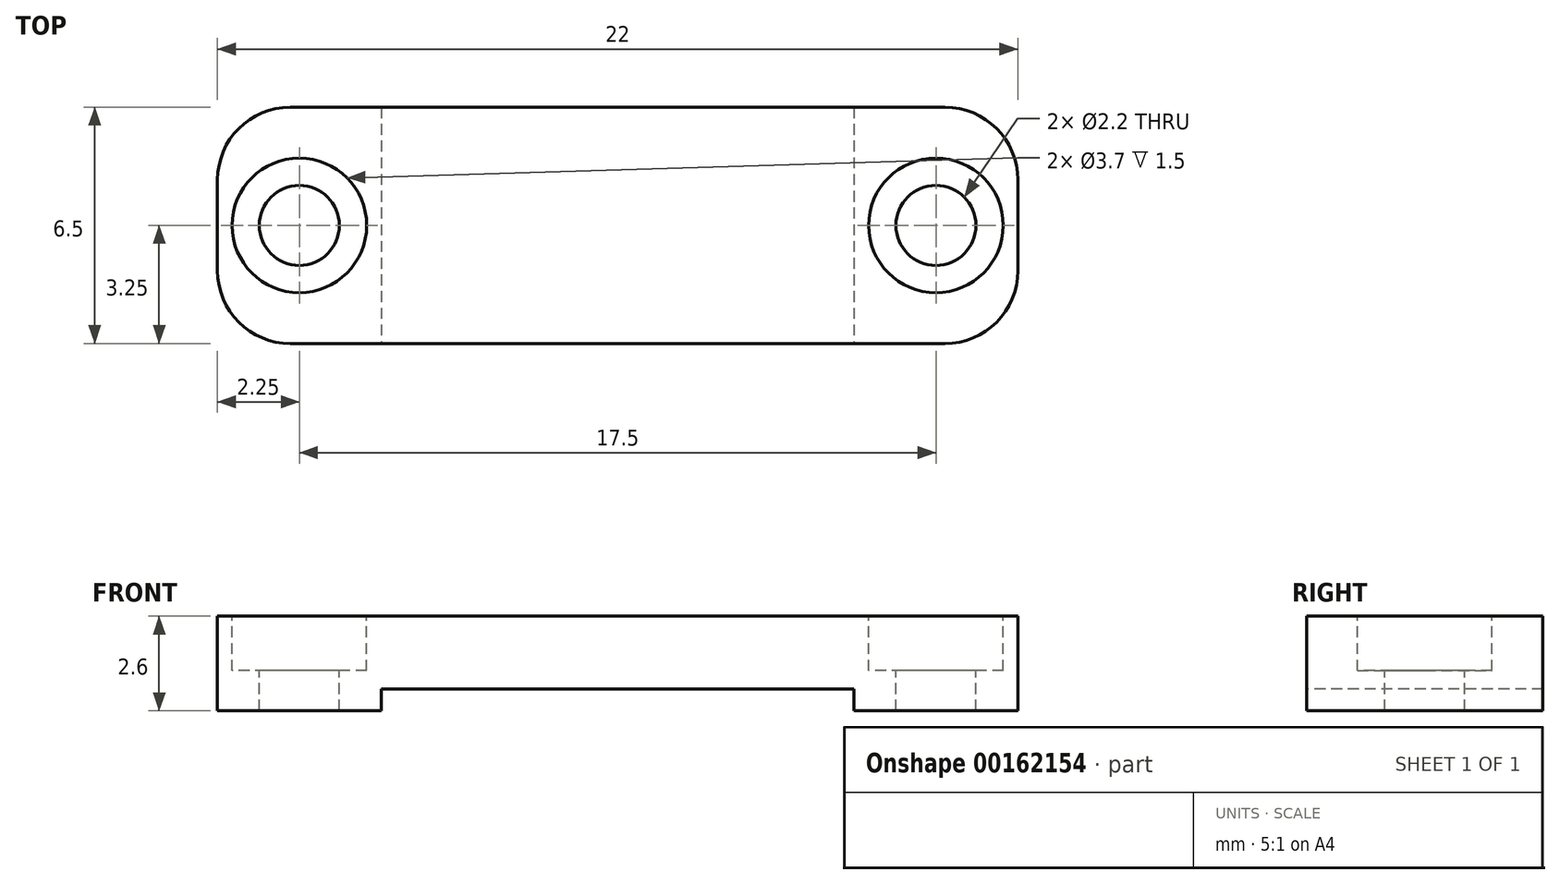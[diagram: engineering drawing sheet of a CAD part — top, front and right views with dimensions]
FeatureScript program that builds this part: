
annotation { "Feature Type Name" : "Feature", "Feature Type Description" : "" }
export const myFeature = defineFeature(function(context is Context, id is Id, definition is map)
    precondition{}
    {
        {
            var Q0;
            Q0=qCreatedBy(makeId("Top.planeOp"),FACE);
            var sketch = newSketch(context, id + "F0", { "sketchPlane" : qUnion([Q0])});
            skLineSegment(sketch, "E0.bottom", {"start": v(-11, 3.25) * mm, "end": v(11, 3.25) * mm});
            skLineSegment(sketch, "E0.top", {"start": v(-11, -3.25) * mm, "end": v(11, -3.25) * mm});
            skLineSegment(sketch, "E0.left", {"start": v(-11, 3.25) * mm, "end": v(-11, -3.25) * mm});
            skLineSegment(sketch, "E0.right", {"start": v(11, 3.25) * mm, "end": v(11, -3.25) * mm});
            skSolve(sketch);
        }
        {
            var Q0;
            Q0 = qSketchRegion(id + "F0", true);
            extrude(context, id + "F1", {"entities" : qUnion([Q0]), "depth" : 2 * mm});
        }
        {
            var Q0;
            Q0=qCreatedBy(makeId("Top.planeOp"),FACE);
            var sketch = newSketch(context, id + "F2", { "sketchPlane" : qUnion([Q0])});
            skLineSegment(sketch, "E1.bottom", {"start": v(-11, 3.25) * mm, "end": v(-6.5, 3.25) * mm});
            skLineSegment(sketch, "E1.top", {"start": v(-11, -3.25) * mm, "end": v(-6.5, -3.25) * mm});
            skLineSegment(sketch, "E1.left", {"start": v(-11, 3.25) * mm, "end": v(-11, -3.25) * mm});
            skLineSegment(sketch, "E1.right", {"start": v(-6.5, 3.25) * mm, "end": v(-6.5, -3.25) * mm});
            skLineSegment(sketch, "E2.bottom", {"start": v(6.5, 3.25) * mm, "end": v(11, 3.25) * mm});
            skLineSegment(sketch, "E2.top", {"start": v(6.5, -3.25) * mm, "end": v(11, -3.25) * mm});
            skLineSegment(sketch, "E2.left", {"start": v(6.5, 3.25) * mm, "end": v(6.5, -3.25) * mm});
            skLineSegment(sketch, "E2.right", {"start": v(11, 3.25) * mm, "end": v(11, -3.25) * mm});
            skSolve(sketch);
        }
        {
            var Q0;
            Q0 = qSketchRegion(id + "F2", true);
            extrude(context, id + "F3", {"entities" : qUnion([Q0]), "operationType" : NewBodyOperationType.ADD, "oppositeDirection" : true, "depth" : 0.6 * mm});
        }
        {
            var Q0;
            Q0=makeQuery(id+"F1.opExtrude","CAP_FACE",FACE,{"disambiguationData":[OSD([sQuery(id+"F0.wireOp",EDGE,"E0.bottom"),sQuery(id+"F0.wireOp",EDGE,"E0.top"),sQuery(id+"F0.wireOp",EDGE,"E0.left"),sQuery(id+"F0.wireOp",EDGE,"E0.right")])],"isStart":false});
            cPlane(context, id + "F4", {"entities" : qUnion([Q0]), "cplaneType" : CPlaneType.OFFSET, "offset" : 0 * mm, "width" : 150 * mm, "height" : 150 * mm});
        }
        {
            var Q0;
            Q0=qCreatedBy(id+"F4.planeOp",FACE);
            var sketch = newSketch(context, id + "F5", { "sketchPlane" : qUnion([Q0])});
            skPoint(sketch, "E3", {"position": v(-8.75, 0) * mm});
            skPoint(sketch, "E4", {"position": v(8.75, 0) * mm});
            skSolve(sketch);
        }
        {
            var Q0;
            Q0=sQuery(id+"F5.wireOp",VERTEX,"E3");
            var Q1;
            Q1=sQuery(id+"F5.wireOp",VERTEX,"E4");
            var Q2;
            Q2=makeQuery(id+"F1.opExtrude","SWEPT_BODY",BODY,{"disambiguationData":[OSD([sQuery(id+"F0.wireOp",EDGE,"E0.bottom"),sQuery(id+"F0.wireOp",EDGE,"E0.top"),sQuery(id+"F0.wireOp",EDGE,"E0.left"),sQuery(id+"F0.wireOp",EDGE,"E0.right")])]});
            hole(context, id + "F6", {"style" : HoleStyle.C_BORE, "endStyle" : HoleEndStyle.THROUGH, "holeDiameter" : 2.2 * mm, "cBoreDiameter" : 3.7 * mm, "cBoreDepth" : 1.5 * mm, "locations" : qUnion([Q0, Q1]), "scope" : qUnion([Q2]), "isTappedThrough" : true});
        }
        {
            var Q0;
            Q0=makeQuery(id+"F3.boolean.opBoolean","MERGE",EDGE,{"derivedFrom":[makeQuery(id+"F1.opExtrude","SWEPT_EDGE",EDGE,{"disambiguationData":[OSD([sQuery(id+"F0.wireOp",EDGE,"E0.top"),sQuery(id+"F0.wireOp",EDGE,"E0.left")])]}),makeQuery(id+"F3.opExtrude","SWEPT_EDGE",EDGE,{"disambiguationData":[OSD([sQuery(id+"F2.wireOp",EDGE,"E1.top"),sQuery(id+"F2.wireOp",EDGE,"E1.left")])]})]});
            var Q1;
            Q1=makeQuery(id+"F3.boolean.opBoolean","MERGE",EDGE,{"derivedFrom":[makeQuery(id+"F1.opExtrude","SWEPT_EDGE",EDGE,{"disambiguationData":[OSD([sQuery(id+"F0.wireOp",EDGE,"E0.bottom"),sQuery(id+"F0.wireOp",EDGE,"E0.left")])]}),makeQuery(id+"F3.opExtrude","SWEPT_EDGE",EDGE,{"disambiguationData":[OSD([sQuery(id+"F2.wireOp",EDGE,"E1.bottom"),sQuery(id+"F2.wireOp",EDGE,"E1.left")])]})]});
            var Q2;
            Q2=makeQuery(id+"F3.boolean.opBoolean","MERGE",EDGE,{"derivedFrom":[makeQuery(id+"F1.opExtrude","SWEPT_EDGE",EDGE,{"disambiguationData":[OSD([sQuery(id+"F0.wireOp",EDGE,"E0.top"),sQuery(id+"F0.wireOp",EDGE,"E0.right")])]}),makeQuery(id+"F3.opExtrude","SWEPT_EDGE",EDGE,{"disambiguationData":[OSD([sQuery(id+"F2.wireOp",EDGE,"E2.top"),sQuery(id+"F2.wireOp",EDGE,"E2.right")])]})]});
            var Q3;
            Q3=makeQuery(id+"F3.boolean.opBoolean","MERGE",EDGE,{"derivedFrom":[makeQuery(id+"F1.opExtrude","SWEPT_EDGE",EDGE,{"disambiguationData":[OSD([sQuery(id+"F0.wireOp",EDGE,"E0.bottom"),sQuery(id+"F0.wireOp",EDGE,"E0.right")])]}),makeQuery(id+"F3.opExtrude","SWEPT_EDGE",EDGE,{"disambiguationData":[OSD([sQuery(id+"F2.wireOp",EDGE,"E2.bottom"),sQuery(id+"F2.wireOp",EDGE,"E2.right")])]})]});
            fillet(context, id + "F7", {"entities" : qUnion([Q0, Q1, Q2, Q3]), "radius" : 2 * mm, "tangentPropagation" : true, "allowEdgeOverflow" : false});
        }
    });
